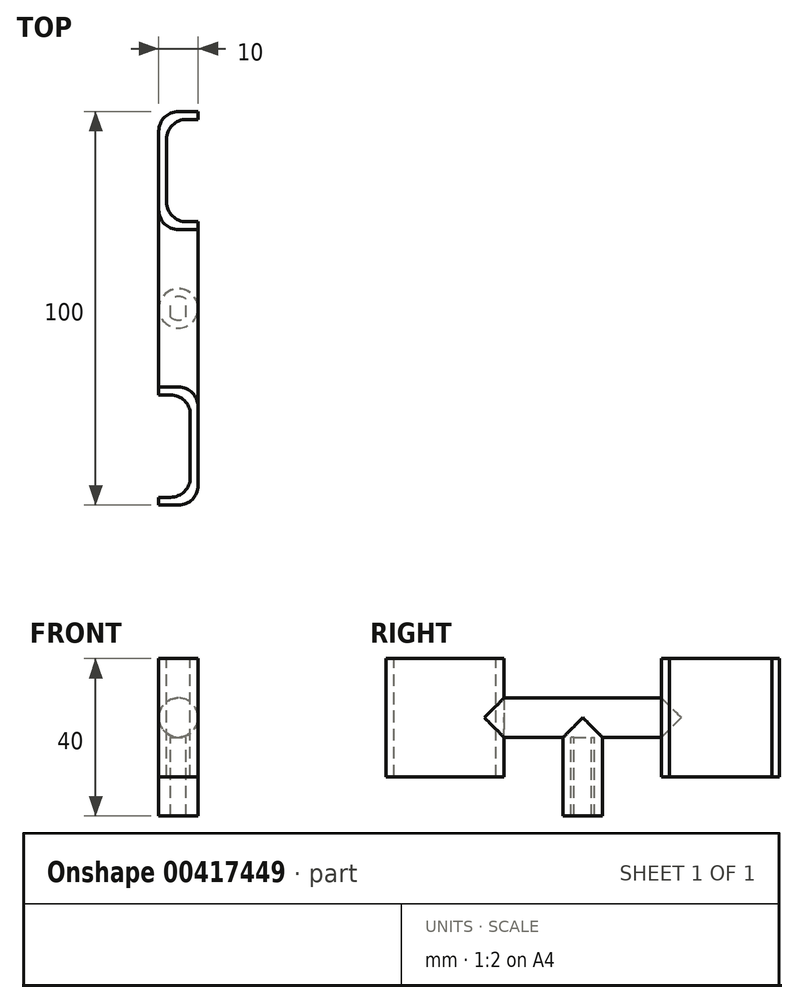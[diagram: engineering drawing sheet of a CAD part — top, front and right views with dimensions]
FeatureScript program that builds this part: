
annotation { "Feature Type Name" : "Feature", "Feature Type Description" : "" }
export const myFeature = defineFeature(function(context is Context, id is Id, definition is map)
    precondition{}
    {
        {
            var Q0;
            Q0=qCreatedBy(makeId("Top.planeOp"),FACE);
            var sketch = newSketch(context, id + "F0", { "sketchPlane" : qUnion([Q0])});
            skLineSegment(sketch, "E0.bottom", {"start": v(5, 50) * mm, "end": v(-5, 50) * mm});
            skLineSegment(sketch, "E0.top", {"start": v(5, -50) * mm, "end": v(-5, -50) * mm});
            skLineSegment(sketch, "E0.left", {"start": v(5, 50) * mm, "end": v(5, -50) * mm});
            skLineSegment(sketch, "E0.right", {"start": v(-5, 50) * mm, "end": v(-5, -50) * mm});
            skPoint(sketch, "E0.middle", {"position": v(0, 0) * mm});
            skSolve(sketch);
        }
        {
            var Q0;
            Q0 = qSketchRegion(id + "F0", true);
            extrude(context, id + "F1", {"entities" : qUnion([Q0]), "depth" : 10 * mm});
        }
        {
            var Q0;
            Q0=makeQuery(id+"F1.opExtrude","CAP_FACE",FACE,{"disambiguationData":[OSD([sQuery(id+"F0.wireOp",EDGE,"E0.bottom"),sQuery(id+"F0.wireOp",EDGE,"E0.top"),sQuery(id+"F0.wireOp",EDGE,"E0.left"),sQuery(id+"F0.wireOp",EDGE,"E0.right")])],"isStart":true});
            var sketch = newSketch(context, id + "F2", { "sketchPlane" : qUnion([Q0])});
            skCircle(sketch, "E1", {"center": v(0, 0) * mm, "radius": 3 * mm});
            skLineSegment(sketch, "E2", {"start": v(-1.98, 2.25) * mm, "end": v(-1.98, -2.25) * mm});
            skLineSegment(sketch, "E3.MirrorCS", {"start": v(1.98, 2.25) * mm, "end": v(1.98, -2.25) * mm});
            skCircle(sketch, "E4", {"center": v(0, 0) * mm, "radius": 5 * mm});
            skSolve(sketch);
        }
        {
            var Q0;
            {var subQ1=sQuery(id+"F2.wireOp",EDGE,"E1");var subQ4=sQuery(id+"F2.wireOp",EDGE,"E2");var subQ6=makeQuery(id+"F2.imprint","INTERSECT",VERTEX,{"disambiguationData":[OD(0.0)],"derivedFrom":[subQ1,subQ4]});Q0=makeQuery(id+"F2.imprint","IMPRINT",FACE,{"disambiguationData":[TD([[makeQuery(id+"F2.imprint","IMPRINT",EDGE,{"disambiguationData":[TD([[subQ6,1.0]])],"derivedFrom":subQ1}),-1.0]])]});}
            var Q1;
            {var subQ0=sQuery(id+"F2.wireOp",EDGE,"E3.MirrorCS");Q1=makeQuery(id+"F2.imprint","IMPRINT",FACE,{"disambiguationData":[TD([[makeQuery(id+"F2.imprint","IMPRINT",EDGE,{"derivedFrom":subQ0}),1.0]])]});}
            var Q2;
            {var subQ0=sQuery(id+"F2.wireOp",EDGE,"E2");Q2=makeQuery(id+"F2.imprint","IMPRINT",FACE,{"disambiguationData":[TD([[makeQuery(id+"F2.imprint","IMPRINT",EDGE,{"derivedFrom":subQ0}),-1.0]])]});}
            extrude(context, id + "F3", {"entities" : qUnion([Q0, Q1, Q2]), "operationType" : NewBodyOperationType.ADD, "depth" : 20 * mm});
        }
        {
            var Q0;
            {var subQ0=sQuery(id+"F0.wireOp",EDGE,"E0.right");var subQ1=sQuery(id+"F0.wireOp",EDGE,"E0.left");var subQ2=sQuery(id+"F0.wireOp",EDGE,"E0.top");var subQ3=makeQuery(id+"F1.opExtrude","CAP_FACE",FACE,{"disambiguationData":[OSD([sQuery(id+"F0.wireOp",EDGE,"E0.bottom"),subQ2,subQ1,subQ0])],"isStart":true});Q0=makeQuery(id+"F3.boolean.opBoolean","SPLIT",FACE,{"disambiguationData":[TD([makeQuery(id+"F1.opExtrude","SWEPT_FACE",FACE,{"disambiguationData":[OSD([subQ2])]})])],"derivedFrom":subQ3});}
            var sketch = newSketch(context, id + "F4", { "sketchPlane" : qUnion([Q0])});
            skLineSegment(sketch, "E5.bottom", {"start": v(-5, 50) * mm, "end": v(5, 50) * mm});
            skLineSegment(sketch, "E5.top", {"start": v(-5, 20) * mm, "end": v(5, 20) * mm});
            skLineSegment(sketch, "E5.left", {"start": v(-5, 50) * mm, "end": v(-5, 20) * mm});
            skLineSegment(sketch, "E5.right", {"start": v(5, 50) * mm, "end": v(5, 20) * mm});
            skSolve(sketch);
        }
        {
            var Q0;
            Q0 = qSketchRegion(id + "F4", true);
            extrude(context, id + "F5", {"entities" : qUnion([Q0]), "operationType" : NewBodyOperationType.ADD, "depth" : 10 * mm});
        }
        {
            var Q0;
            Q0=makeQuery(id+"F1.opExtrude","CAP_FACE",FACE,{"disambiguationData":[OSD([sQuery(id+"F0.wireOp",EDGE,"E0.bottom"),sQuery(id+"F0.wireOp",EDGE,"E0.top"),sQuery(id+"F0.wireOp",EDGE,"E0.left"),sQuery(id+"F0.wireOp",EDGE,"E0.right")])],"isStart":false});
            var sketch = newSketch(context, id + "F6", { "sketchPlane" : qUnion([Q0])});
            skLineSegment(sketch, "E6.bottom", {"start": v(5, -50) * mm, "end": v(-5, -50) * mm});
            skLineSegment(sketch, "E6.top", {"start": v(5, -20) * mm, "end": v(-5, -20) * mm});
            skLineSegment(sketch, "E6.left", {"start": v(5, -50) * mm, "end": v(5, -20) * mm});
            skLineSegment(sketch, "E6.right", {"start": v(-5, -50) * mm, "end": v(-5, -20) * mm});
            skSolve(sketch);
        }
        {
            var Q0;
            Q0 = qSketchRegion(id + "F6", true);
            extrude(context, id + "F7", {"entities" : qUnion([Q0]), "operationType" : NewBodyOperationType.ADD, "depth" : 10 * mm});
        }
        {
            var Q0;
            Q0=makeQuery(id+"F7.opExtrude","CAP_FACE",FACE,{"disambiguationData":[OSD([sQuery(id+"F6.wireOp",EDGE,"E6.bottom"),sQuery(id+"F6.wireOp",EDGE,"E6.top"),sQuery(id+"F6.wireOp",EDGE,"E6.left"),sQuery(id+"F6.wireOp",EDGE,"E6.right")])],"isStart":false});
            var sketch = newSketch(context, id + "F8", { "sketchPlane" : qUnion([Q0])});
            skLineSegment(sketch, "E7.bottom", {"start": v(-5, -22) * mm, "end": v(3, -22) * mm});
            skLineSegment(sketch, "E7.top", {"start": v(-5, -48) * mm, "end": v(3, -48) * mm});
            skLineSegment(sketch, "E7.left", {"start": v(-5, -22) * mm, "end": v(-5, -48) * mm});
            skLineSegment(sketch, "E7.right", {"start": v(3, -22) * mm, "end": v(3, -48) * mm});
            skSolve(sketch);
        }
        {
            var Q0;
            Q0=makeQuery(id+"F8.imprint","IMPRINT",FACE,{"disambiguationData":[TD([[makeQuery(id+"F8.imprint","IMPRINT",EDGE,{"derivedFrom":sQuery(id+"F8.wireOp",EDGE,"E7.bottom")}),-1.0]])]});
            extrude(context, id + "F9", {"entities" : qUnion([Q0]), "operationType" : NewBodyOperationType.REMOVE, "oppositeDirection" : true, "depth" : 30 * mm});
        }
        {
            var Q0;
            Q0=makeQuery(id+"F9.boolean.opBoolean","COPY",EDGE,{"derivedFrom":makeQuery(id+"F9.opExtrude","SWEPT_EDGE",EDGE,{"disambiguationData":[OSD([sQuery(id+"F8.wireOp",EDGE,"E7.bottom"),sQuery(id+"F8.wireOp",EDGE,"E7.right")])]})});
            var Q1;
            Q1=makeQuery(id+"F9.boolean.opBoolean","COPY",EDGE,{"derivedFrom":makeQuery(id+"F9.opExtrude","SWEPT_EDGE",EDGE,{"disambiguationData":[OSD([sQuery(id+"F8.wireOp",EDGE,"E7.top"),sQuery(id+"F8.wireOp",EDGE,"E7.right")])]})});
            var Q2;
            Q2=makeQuery(id+"F5.opExtrude","SWEPT_EDGE",EDGE,{"disambiguationData":[OSD([sQuery(id+"F0.wireOp",EDGE,"E0.left"),sQuery(id+"F4.wireOp",EDGE,"E5.top"),sQuery(id+"F4.wireOp",EDGE,"E5.right")])]});
            var Q3;
            Q3=makeQuery(id+"F7.opExtrude","SWEPT_EDGE",EDGE,{"disambiguationData":[OSD([sQuery(id+"F0.wireOp",EDGE,"E0.left"),sQuery(id+"F6.wireOp",EDGE,"E6.top"),sQuery(id+"F6.wireOp",EDGE,"E6.left")])]});
            var Q4;
            Q4=makeQuery(id+"F7.boolean.opBoolean","MERGE",EDGE,{"derivedFrom":[makeQuery(id+"F5.boolean.opBoolean","MERGE",EDGE,{"derivedFrom":[makeQuery(id+"F1.opExtrude","SWEPT_EDGE",EDGE,{"disambiguationData":[OSD([sQuery(id+"F0.wireOp",EDGE,"E0.top"),sQuery(id+"F0.wireOp",EDGE,"E0.left")])]}),makeQuery(id+"F5.opExtrude","SWEPT_EDGE",EDGE,{"disambiguationData":[OSD([sQuery(id+"F4.wireOp",EDGE,"E5.bottom"),sQuery(id+"F4.wireOp",EDGE,"E5.right")])]})]}),makeQuery(id+"F7.opExtrude","SWEPT_EDGE",EDGE,{"disambiguationData":[OSD([sQuery(id+"F6.wireOp",EDGE,"E6.bottom"),sQuery(id+"F6.wireOp",EDGE,"E6.left")])]})]});
            fillet(context, id + "F10", {"entities" : qUnion([Q0, Q1, Q2, Q3, Q4]), "radius" : 5 * mm, "tangentPropagation" : true, "allowEdgeOverflow" : false});
        }
        {
            var Q0;
            {var subQ0=sQuery(id+"F0.wireOp",EDGE,"E0.left");var subQ1=sQuery(id+"F0.wireOp",EDGE,"E0.right");var subQ2=sQuery(id+"F0.wireOp",EDGE,"E0.bottom");var subQ3=makeQuery(id+"F1.opExtrude","CAP_FACE",FACE,{"disambiguationData":[OSD([subQ2,sQuery(id+"F0.wireOp",EDGE,"E0.top"),subQ0,subQ1])],"isStart":true});Q0=makeQuery(id+"F3.boolean.opBoolean","SPLIT",FACE,{"disambiguationData":[TD([makeQuery(id+"F1.opExtrude","SWEPT_FACE",FACE,{"disambiguationData":[OSD([subQ2])]})])],"derivedFrom":subQ3});}
            var sketch = newSketch(context, id + "F11", { "sketchPlane" : qUnion([Q0])});
            skLineSegment(sketch, "E8.bottom", {"start": v(5, -50) * mm, "end": v(-5, -50) * mm});
            skLineSegment(sketch, "E8.top", {"start": v(5, -20) * mm, "end": v(-5, -20) * mm});
            skLineSegment(sketch, "E8.left", {"start": v(5, -50) * mm, "end": v(5, -20) * mm});
            skLineSegment(sketch, "E8.right", {"start": v(-5, -50) * mm, "end": v(-5, -20) * mm});
            skSolve(sketch);
        }
        {
            var Q0;
            Q0 = qSketchRegion(id + "F11", true);
            extrude(context, id + "F12", {"entities" : qUnion([Q0]), "operationType" : NewBodyOperationType.ADD, "depth" : 10 * mm});
        }
        {
            var Q0;
            Q0=makeQuery(id+"F1.opExtrude","CAP_FACE",FACE,{"disambiguationData":[OSD([sQuery(id+"F0.wireOp",EDGE,"E0.bottom"),sQuery(id+"F0.wireOp",EDGE,"E0.top"),sQuery(id+"F0.wireOp",EDGE,"E0.left"),sQuery(id+"F0.wireOp",EDGE,"E0.right")])],"isStart":false});
            var sketch = newSketch(context, id + "F13", { "sketchPlane" : qUnion([Q0])});
            skLineSegment(sketch, "E9.bottom", {"start": v(-5, 50) * mm, "end": v(5, 50) * mm});
            skLineSegment(sketch, "E9.top", {"start": v(-5, 20) * mm, "end": v(5, 20) * mm});
            skLineSegment(sketch, "E9.left", {"start": v(-5, 50) * mm, "end": v(-5, 20) * mm});
            skLineSegment(sketch, "E9.right", {"start": v(5, 50) * mm, "end": v(5, 20) * mm});
            skSolve(sketch);
        }
        {
            var Q0;
            Q0 = qSketchRegion(id + "F13", true);
            extrude(context, id + "F14", {"entities" : qUnion([Q0]), "operationType" : NewBodyOperationType.ADD, "depth" : 10 * mm});
        }
        {
            var Q0;
            Q0=makeQuery(id+"F14.opExtrude","CAP_FACE",FACE,{"disambiguationData":[OSD([sQuery(id+"F13.wireOp",EDGE,"E9.bottom"),sQuery(id+"F13.wireOp",EDGE,"E9.top"),sQuery(id+"F13.wireOp",EDGE,"E9.left"),sQuery(id+"F13.wireOp",EDGE,"E9.right")])],"isStart":false});
            var sketch = newSketch(context, id + "F15", { "sketchPlane" : qUnion([Q0])});
            skLineSegment(sketch, "E10.bottom", {"start": v(5, 48) * mm, "end": v(-3, 48) * mm});
            skLineSegment(sketch, "E10.top", {"start": v(5, 22) * mm, "end": v(-3, 22) * mm});
            skLineSegment(sketch, "E10.left", {"start": v(5, 48) * mm, "end": v(5, 22) * mm});
            skLineSegment(sketch, "E10.right", {"start": v(-3, 48) * mm, "end": v(-3, 22) * mm});
            skSolve(sketch);
        }
        {
            var Q0;
            Q0 = qSketchRegion(id + "F15", true);
            extrude(context, id + "F16", {"entities" : qUnion([Q0]), "operationType" : NewBodyOperationType.REMOVE, "oppositeDirection" : true, "depth" : 30 * mm});
        }
        {
            var Q0;
            Q0=makeQuery(id+"F16.boolean.opBoolean","COPY",EDGE,{"derivedFrom":makeQuery(id+"F16.opExtrude","SWEPT_EDGE",EDGE,{"disambiguationData":[OSD([sQuery(id+"F15.wireOp",EDGE,"E10.bottom"),sQuery(id+"F15.wireOp",EDGE,"E10.right")])]})});
            var Q1;
            Q1=makeQuery(id+"F14.boolean.opBoolean","MERGE",EDGE,{"derivedFrom":[makeQuery(id+"F12.boolean.opBoolean","MERGE",EDGE,{"derivedFrom":[makeQuery(id+"F1.opExtrude","SWEPT_EDGE",EDGE,{"disambiguationData":[OSD([sQuery(id+"F0.wireOp",EDGE,"E0.bottom"),sQuery(id+"F0.wireOp",EDGE,"E0.right")])]}),makeQuery(id+"F12.opExtrude","SWEPT_EDGE",EDGE,{"disambiguationData":[OSD([sQuery(id+"F11.wireOp",EDGE,"E8.bottom"),sQuery(id+"F11.wireOp",EDGE,"E8.right")])]})]}),makeQuery(id+"F14.opExtrude","SWEPT_EDGE",EDGE,{"disambiguationData":[OSD([sQuery(id+"F13.wireOp",EDGE,"E9.bottom"),sQuery(id+"F13.wireOp",EDGE,"E9.left")])]})]});
            var Q2;
            Q2=makeQuery(id+"F14.opExtrude","SWEPT_EDGE",EDGE,{"disambiguationData":[OSD([sQuery(id+"F0.wireOp",EDGE,"E0.right"),sQuery(id+"F13.wireOp",EDGE,"E9.top"),sQuery(id+"F13.wireOp",EDGE,"E9.left")])]});
            var Q3;
            Q3=makeQuery(id+"F12.opExtrude","SWEPT_EDGE",EDGE,{"disambiguationData":[OSD([sQuery(id+"F0.wireOp",EDGE,"E0.right"),sQuery(id+"F11.wireOp",EDGE,"E8.top"),sQuery(id+"F11.wireOp",EDGE,"E8.right")])]});
            var Q4;
            Q4=makeQuery(id+"F16.boolean.opBoolean","COPY",EDGE,{"derivedFrom":makeQuery(id+"F16.opExtrude","SWEPT_EDGE",EDGE,{"disambiguationData":[OSD([sQuery(id+"F15.wireOp",EDGE,"E10.top"),sQuery(id+"F15.wireOp",EDGE,"E10.right")])]})});
            var Q5;
            {var subQ0=sQuery(id+"F0.wireOp",EDGE,"E0.left");var subQ1=sQuery(id+"F0.wireOp",EDGE,"E0.top");Q5=makeQuery(id+"F3.boolean.opBoolean","SPLIT",EDGE,{"disambiguationData":[TD([makeQuery(id+"F1.opExtrude","SWEPT_FACE",FACE,{"disambiguationData":[OSD([subQ1])]})])],"derivedFrom":makeQuery(id+"F1.opExtrude","CAP_EDGE",EDGE,{"disambiguationData":[OSD([subQ0])],"isStart":true})});}
            var Q6;
            Q6=makeQuery(id+"F1.opExtrude","CAP_EDGE",EDGE,{"disambiguationData":[OSD([sQuery(id+"F0.wireOp",EDGE,"E0.left")])],"isStart":false});
            var Q7;
            {var subQ0=sQuery(id+"F0.wireOp",EDGE,"E0.bottom");var subQ1=sQuery(id+"F0.wireOp",EDGE,"E0.right");Q7=makeQuery(id+"F3.boolean.opBoolean","SPLIT",EDGE,{"disambiguationData":[TD([makeQuery(id+"F1.opExtrude","SWEPT_FACE",FACE,{"disambiguationData":[OSD([subQ0])]})])],"derivedFrom":makeQuery(id+"F1.opExtrude","CAP_EDGE",EDGE,{"disambiguationData":[OSD([subQ1])],"isStart":true})});}
            var Q8;
            Q8=makeQuery(id+"F1.opExtrude","CAP_EDGE",EDGE,{"disambiguationData":[OSD([sQuery(id+"F0.wireOp",EDGE,"E0.right")])],"isStart":false});
            fillet(context, id + "F17", {"entities" : qUnion([Q0, Q1, Q2, Q3, Q4, Q5, Q6, Q7, Q8]), "radius" : 5 * mm, "tangentPropagation" : true, "allowEdgeOverflow" : false});
        }
    });
